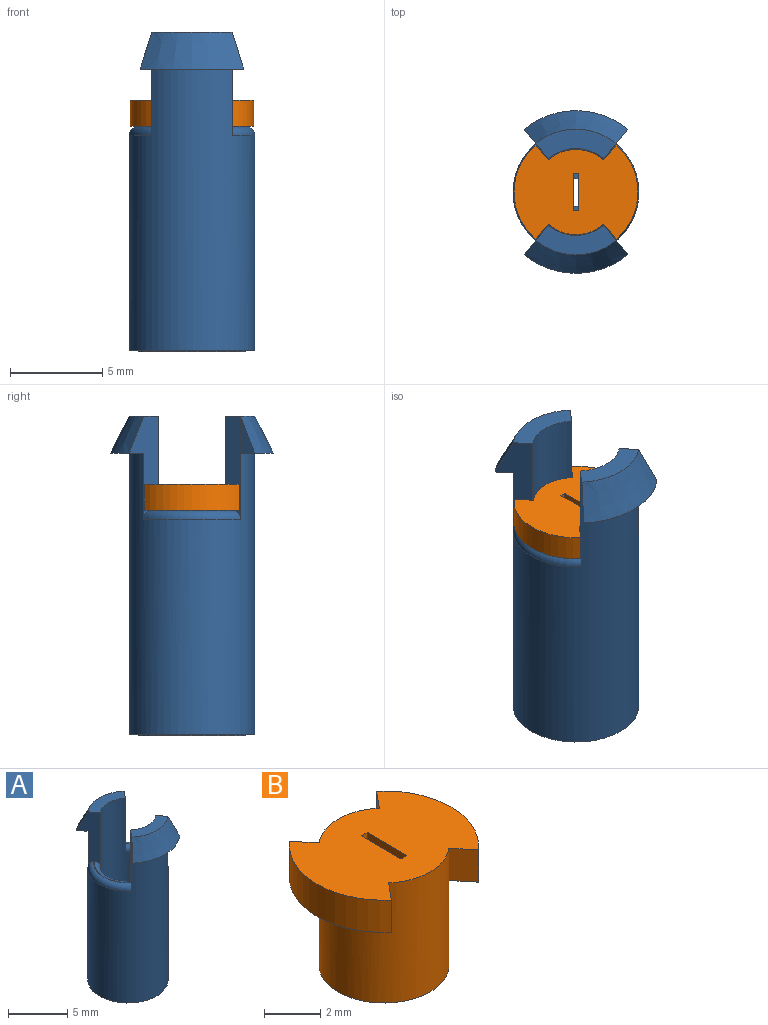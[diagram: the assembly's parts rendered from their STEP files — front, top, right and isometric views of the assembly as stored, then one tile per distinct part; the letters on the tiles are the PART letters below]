
ASSEMBLY  parts=2 mates=1
PART A: 27 faces, bbox 7.4x8.8x17.4 mm
  f0: cylinder r=3.4mm len=15.2mm, axis (0,0,-1), area 281.7mm2, adj f3,f10,f11,f13,f14,f16,f20,f23
  f1: plane 4.46x1.08mm, normal (0,0,1), area 0.3mm2, adj f11,f14,f25,f26
  f2: plane 4.46x1.08mm, normal (0,0,1), area 0.3mm2, adj f10,f13,f23,f24
  f3: plane 6.8x6.8mm, normal (0,0,-1), area 9.9mm2, adj f0,f7
  f4: cylinder r=2.35mm len=16.2mm, axis (0,0,-1), area 193mm2, adj f5,f10,f11,f12,f13,f14,f15,f24
  f5: plane 4.7x4.7mm, normal (0,0,1), area 15.6mm2, adj f4,f9
  f6: cylinder r=0.9mm len=1.8mm, axis (0,0,1), area 0.6mm2, adj f8,f22
  f7: cylinder r=2.9mm len=5.8mm, axis (0,0,1), area 1.8mm2, adj f3,f8
  f8: plane 5.8x5.8mm, normal (0,0,-1), area 23.9mm2, adj f6,f7
  f9: cylinder r=0.75mm len=1.5mm, axis (0,0,-1), area 3mm2, adj f5,f22
  f10: plane 5.62x0.83mm, normal (0.77,-0.64,0), area 5.5mm2, adj f0,f2,f4,f12,f18,f23,f24
  f11: plane 5.6x1.58mm, normal (-0.77,-0.64,0), area 6.5mm2, adj f0,f1,f4,f12,f16,f17,f25,f26
  f12: plane 4.34x1.59mm, normal (0,0,1), area 4.2mm2, adj f4,f10,f11,f17
  f13: plane 5.6x1.58mm, normal (0.77,0.64,0), area 6.5mm2, adj f0,f2,f4,f15,f19,f20,f23,f24
  f14: plane 5.62x0.83mm, normal (-0.77,0.64,0), area 5.5mm2, adj f0,f1,f4,f15,f21,f25,f26
  f15: plane 4.34x1.59mm, normal (0,0,1), area 4.2mm2, adj f4,f13,f14,f19
  f16: plane 5.61x1.78mm, normal (0,0,-1), area 5.4mm2, adj f0,f11,f17,f18
  f17: cone r=4.4mm half-angle=26.6deg, axis (0,0,-1), area 12.1mm2, adj f11,f12,f16,f18
  f18: plane 2.02x0.79mm, normal (0.77,-0.64,0), area 1mm2, adj f10,f16,f17
  f19: cone r=4.4mm half-angle=26.6deg, axis (0,0,-1), area 12.1mm2, adj f13,f15,f20,f21
  f20: plane 5.61x1.78mm, normal (0,0,-1), area 5.4mm2, adj f0,f13,f19,f21
  f21: plane 2.02x0.79mm, normal (-0.77,0.64,0), area 1mm2, adj f14,f19,f20
  f22: torus R=1.25mm, axis (0,0,-1), area 2mm2, adj f6,f9
  f23: torus R=2.9mm, axis (0,0,1), area 4.4mm2, adj f0,f2,f10,f13
  f24: torus R=2.85mm, axis (0,0,1), area 3.5mm2, adj f2,f4,f10,f13
  f25: torus R=2.85mm, axis (0,0,1), area 3.5mm2, adj f1,f4,f11,f14
  f26: torus R=2.9mm, axis (0,0,1), area 4.4mm2, adj f0,f1,f11,f14
PART B: 21 faces, bbox 6.7x5.1x5.2 mm
  f0: plane 4.6x4.6mm, normal (0,0,-1), area 9.1mm2, adj f6,f11,f13,f14,f15,f16
  f1: plane 5.09x1.84mm, normal (0,0,-1), area 5.1mm2, adj f3,f4,f5,f6
  f2: plane 1.4x0.81mm, normal (-0.77,0.64,0), area 1.5mm2, adj f6,f8,f9,f10
  f3: plane 1.4x0.81mm, normal (0.77,0.64,0), area 1.5mm2, adj f1,f4,f6,f9
  f4: cylinder r=3.35mm len=5.09mm, axis (0,0,-1), area 8.1mm2, adj f1,f3,f5,f9
  f5: plane 1.4x0.81mm, normal (0.77,-0.64,0), area 1.5mm2, adj f1,f4,f6,f9
  f6: cylinder r=2.3mm len=5.2mm, axis (0,0,-1), area 49.1mm2, adj f0,f1,f2,f3,f5,f7,f9,f11
  f7: plane 1.4x0.81mm, normal (-0.77,-0.64,0), area 1.5mm2, adj f6,f8,f9,f10
  f8: cylinder r=3.35mm len=5.09mm, axis (0,0,-1), area 8.1mm2, adj f2,f7,f9,f10
  f9: plane 6.7x5.09mm, normal (0,0,1), area 26.2mm2, adj f2,f3,f4,f5,f6,f7,f8,f17
  f10: plane 5.09x1.84mm, normal (0,0,-1), area 5.1mm2, adj f2,f7,f8,f11
  f11: extruded ~3.8x3.48mm, area 15mm2, adj f0,f6,f10
  f12: plane 3x2.5mm, normal (0,0,-1), area 6.9mm2, adj f13,f14,f15,f16,f17,f18,f19,f20
  f13: plane 3.8x2.5mm, normal (0,1,0), area 9.5mm2, adj f0,f12,f14,f16
  f14: plane 3.8x3mm, normal (1,0,0), area 11.4mm2, adj f0,f12,f13,f15
  f15: plane 3.8x2.5mm, normal (0,-1,0), area 9.5mm2, adj f0,f12,f14,f16
  f16: plane 3.8x3mm, normal (-1,0,0), area 11.4mm2, adj f0,f12,f13,f15
  f17: plane 2x1.4mm, normal (1,0,0), area 2.8mm2, adj f9,f12,f18,f19
  f18: plane 1.4x0.3mm, normal (0,-1,0), area 0.4mm2, adj f9,f12,f17,f20
  f19: plane 1.4x0.3mm, normal (0,1,0), area 0.4mm2, adj f9,f12,f17,f20
  f20: plane 2x1.4mm, normal (-1,0,0), area 2.8mm2, adj f9,f12,f18,f19
PLACE A at identity fixed
PLACE B at identity
MATE fastened A.f0 <-> B.f4  axis (0,0,1) through (0,0,12.1)mm
